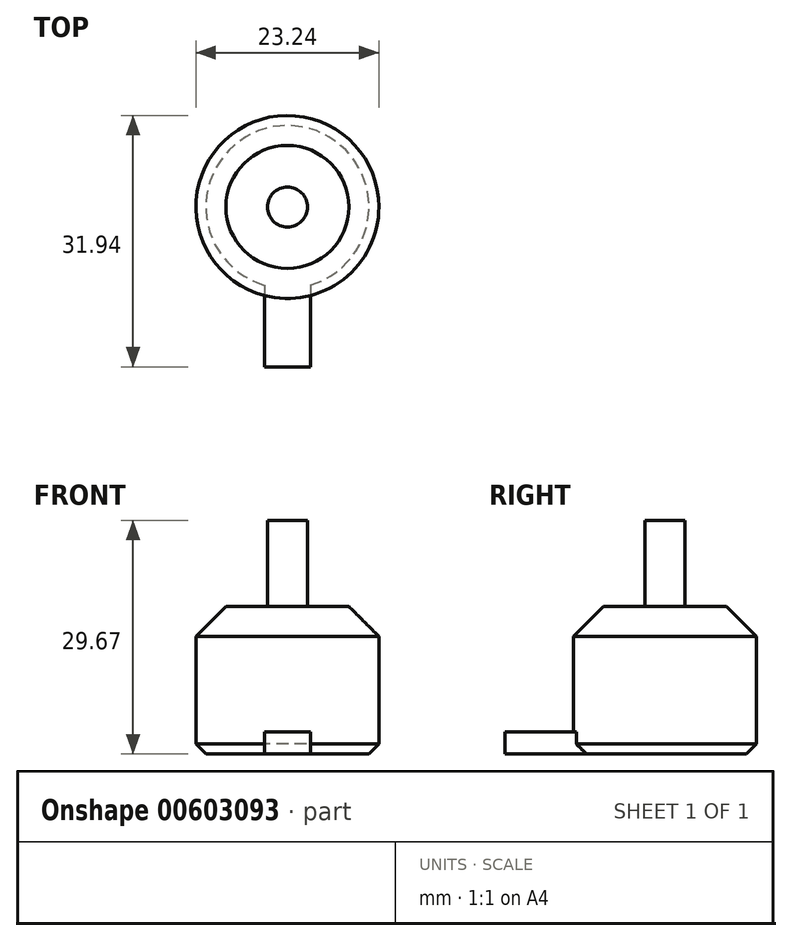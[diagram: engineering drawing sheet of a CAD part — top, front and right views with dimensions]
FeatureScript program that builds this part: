
annotation { "Feature Type Name" : "Feature", "Feature Type Description" : "" }
export const myFeature = defineFeature(function(context is Context, id is Id, definition is map)
    precondition{}
    {
        {
            var Q0;
            Q0=qCreatedBy(makeId("Top.planeOp"),FACE);
            var sketch = newSketch(context, id + "F0", { "sketchPlane" : qUnion([Q0])});
            skCircle(sketch, "E0", {"center": v(0, 0) * mm, "radius": 11.62 * mm});
            skSolve(sketch);
        }
        {
            var Q0;
            Q0 = qSketchRegion(id + "F0", true);
            extrude(context, id + "F1", {"entities" : qUnion([Q0]), "depth" : 18.75 * mm, "offsetDistance" : 25.4 * mm});
        }
        {
            var Q0;
            Q0=makeQuery(id+"F1.opExtrude","CAP_FACE",FACE,{"disambiguationData":[OSD([sQuery(id+"F0.wireOp",EDGE,"E0")])],"isStart":false});
            var sketch = newSketch(context, id + "F2", { "sketchPlane" : qUnion([Q0])});
            skCircle(sketch, "E1", {"center": v(0, 0) * mm, "radius": 2.54 * mm});
            skSolve(sketch);
        }
        {
            var Q0;
            Q0 = qSketchRegion(id + "F2", true);
            extrude(context, id + "F3", {"entities" : qUnion([Q0]), "operationType" : NewBodyOperationType.ADD, "depth" : 10.92 * mm, "offsetDistance" : 25.4 * mm});
        }
        {
            var Q0;
            Q0=makeQuery(id+"F1.opExtrude","CAP_EDGE",EDGE,{"disambiguationData":[OSD([sQuery(id+"F0.wireOp",EDGE,"E0")])],"isStart":false});
            chamfer(context, id + "F4", {"entities" : qUnion([Q0]), "width" : 3.8 * mm, "tangentPropagation" : true});
        }
        {
            var Q0;
            Q0=makeQuery(id+"F1.opExtrude","CAP_EDGE",EDGE,{"disambiguationData":[OSD([sQuery(id+"F0.wireOp",EDGE,"E0")])],"isStart":true});
            chamfer(context, id + "F5", {"entities" : qUnion([Q0]), "width" : 1.27 * mm, "tangentPropagation" : true});
        }
        {
            var Q0;
            Q0=makeQuery(id+"F1.opExtrude","CAP_FACE",FACE,{"disambiguationData":[OSD([sQuery(id+"F0.wireOp",EDGE,"E0")])],"isStart":true});
            var sketch = newSketch(context, id + "F6", { "sketchPlane" : qUnion([Q0])});
            skLineSegment(sketch, "E2.bottom", {"start": v(-2.92, 0) * mm, "end": v(2.92, 0) * mm});
            skLineSegment(sketch, "E2.top", {"start": v(-2.92, 20.32) * mm, "end": v(2.92, 20.32) * mm});
            skLineSegment(sketch, "E2.left", {"start": v(-2.92, 0) * mm, "end": v(-2.92, 20.32) * mm});
            skLineSegment(sketch, "E2.right", {"start": v(2.92, 0) * mm, "end": v(2.92, 20.32) * mm});
            skSolve(sketch);
        }
        {
            var Q0;
            Q0 = qSketchRegion(id + "F6", true);
            extrude(context, id + "F7", {"entities" : qUnion([Q0]), "operationType" : NewBodyOperationType.ADD, "oppositeDirection" : true, "depth" : 2.8 * mm, "offsetDistance" : 25.4 * mm});
        }
    });
